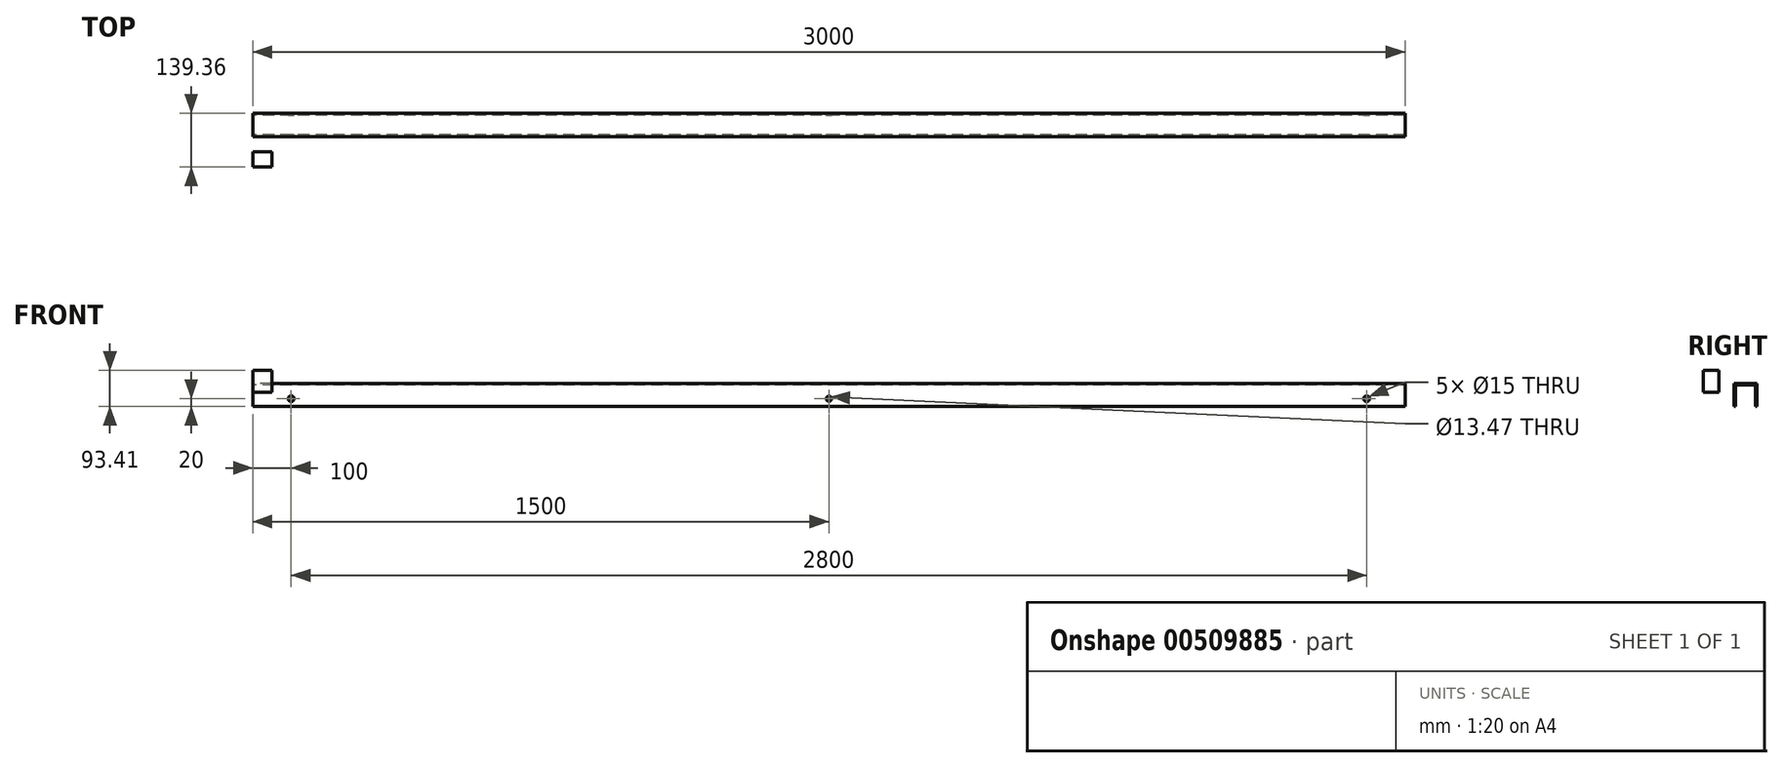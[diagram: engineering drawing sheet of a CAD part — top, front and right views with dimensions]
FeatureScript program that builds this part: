
annotation { "Feature Type Name" : "Feature", "Feature Type Description" : "" }
export const myFeature = defineFeature(function(context is Context, id is Id, definition is map)
    precondition{}
    {
        {
            var Q0;
            Q0=qCreatedBy(makeId("Right.planeOp"),FACE);
            var sketch = newSketch(context, id + "F0", { "sketchPlane" : qUnion([Q0])});
            skLineSegment(sketch, "E0", {"start": v(0, 0) * mm, "end": v(60, 0) * mm});
            skLineSegment(sketch, "E1", {"start": v(60, 0) * mm, "end": v(60, -60) * mm});
            skLineSegment(sketch, "E2", {"start": v(60, -60) * mm, "end": v(56, -60) * mm});
            skLineSegment(sketch, "E3", {"start": v(56, -60) * mm, "end": v(56, -4) * mm});
            skLineSegment(sketch, "E4", {"start": v(56, -4) * mm, "end": v(4, -4) * mm});
            skLineSegment(sketch, "E5", {"start": v(4, -4) * mm, "end": v(4, -60) * mm});
            skLineSegment(sketch, "E6", {"start": v(4, -60) * mm, "end": v(0, -60) * mm});
            skLineSegment(sketch, "E7", {"start": v(0, -60) * mm, "end": v(0, 0) * mm});
            skSolve(sketch);
        }
        {
            var Q0;
            Q0=makeQuery(id+"F0.imprint","IMPRINT",FACE,{"disambiguationData":[TD([[makeQuery(id+"F0.imprint","IMPRINT",EDGE,{"derivedFrom":sQuery(id+"F0.wireOp",EDGE,"E0")}),-1.0]])]});
            extrude(context, id + "F1", {"entities" : qUnion([Q0]), "depth" : 3000 * mm, "offsetDistance" : 25 * mm});
        }
        {
            var Q0;
            Q0=makeQuery(id+"F1.opExtrude","SWEPT_FACE",FACE,{"disambiguationData":[OSD([sQuery(id+"F0.wireOp",EDGE,"E1")])]});
            var sketch = newSketch(context, id + "F2", { "sketchPlane" : qUnion([Q0])});
            skCircle(sketch, "E8", {"center": v(-2900, -40) * mm, "radius": 7.5 * mm});
            skCircle(sketch, "E9", {"center": v(-1500, -40) * mm, "radius": 7.5 * mm});
            skCircle(sketch, "E10", {"center": v(-100, -40) * mm, "radius": 7.5 * mm});
            skSolve(sketch);
        }
        {
            var Q0;
            Q0=makeQuery(id+"F2.imprint","IMPRINT",FACE,{"disambiguationData":[TD([[makeQuery(id+"F2.imprint","IMPRINT",EDGE,{"derivedFrom":sQuery(id+"F2.wireOp",EDGE,"E10")}),1.0]])]});
            extrude(context, id + "F3", {"entities" : qUnion([Q0]), "operationType" : NewBodyOperationType.REMOVE, "oppositeDirection" : true, "depth" : 4 * mm, "offsetDistance" : 25 * mm});
        }
        {
            var Q0;
            Q0=makeQuery(id+"F1.opExtrude","SWEPT_FACE",FACE,{"disambiguationData":[OSD([sQuery(id+"F0.wireOp",EDGE,"E1")])]});
            var sketch = newSketch(context, id + "F4", { "sketchPlane" : qUnion([Q0])});
            skCircle(sketch, "E11", {"center": v(-2900, -40) * mm, "radius": 7.5 * mm});
            skSolve(sketch);
        }
        {
            var Q0;
            Q0=makeQuery(id+"F4.imprint","IMPRINT",FACE,{"disambiguationData":[TD([[makeQuery(id+"F4.imprint","IMPRINT",EDGE,{"derivedFrom":sQuery(id+"F4.wireOp",EDGE,"E11")}),1.0]])]});
            extrude(context, id + "F5", {"entities" : qUnion([Q0]), "operationType" : NewBodyOperationType.REMOVE, "oppositeDirection" : true, "depth" : 4 * mm, "offsetDistance" : 25 * mm});
        }
        {
            var Q0;
            Q0=makeQuery(id+"F1.opExtrude","SWEPT_FACE",FACE,{"disambiguationData":[OSD([sQuery(id+"F0.wireOp",EDGE,"E1")])]});
            var sketch = newSketch(context, id + "F6", { "sketchPlane" : qUnion([Q0])});
            skCircle(sketch, "E12", {"center": v(-1500, -40) * mm, "radius": 7.5 * mm});
            skSolve(sketch);
        }
        {
            var Q0;
            Q0=makeQuery(id+"F6.imprint","IMPRINT",FACE,{"disambiguationData":[TD([[makeQuery(id+"F6.imprint","IMPRINT",EDGE,{"derivedFrom":sQuery(id+"F6.wireOp",EDGE,"E12")}),1.0]])]});
            extrude(context, id + "F7", {"entities" : qUnion([Q0]), "operationType" : NewBodyOperationType.REMOVE, "oppositeDirection" : true, "depth" : 4 * mm, "offsetDistance" : 25 * mm});
        }
        {
            var Q0;
            Q0=makeQuery(id+"F1.opExtrude","SWEPT_FACE",FACE,{"disambiguationData":[OSD([sQuery(id+"F0.wireOp",EDGE,"E7")])]});
            var sketch = newSketch(context, id + "F8", { "sketchPlane" : qUnion([Q0])});
            skCircle(sketch, "E13", {"center": v(100, -40) * mm, "radius": 7.5 * mm});
            skSolve(sketch);
        }
        {
            var Q0;
            Q0=makeQuery(id+"F8.imprint","IMPRINT",FACE,{"disambiguationData":[TD([[makeQuery(id+"F8.imprint","IMPRINT",EDGE,{"derivedFrom":sQuery(id+"F8.wireOp",EDGE,"E13")}),1.0]])]});
            extrude(context, id + "F9", {"entities" : qUnion([Q0]), "operationType" : NewBodyOperationType.REMOVE, "oppositeDirection" : true, "depth" : 4 * mm, "offsetDistance" : 25 * mm});
        }
        {
            var Q0;
            Q0=makeQuery(id+"F1.opExtrude","SWEPT_FACE",FACE,{"disambiguationData":[OSD([sQuery(id+"F0.wireOp",EDGE,"E7")])]});
            var sketch = newSketch(context, id + "F10", { "sketchPlane" : qUnion([Q0])});
            skCircle(sketch, "E14", {"center": v(1500, -40) * mm, "radius": 6.74 * mm});
            skSolve(sketch);
        }
        {
            var Q0;
            Q0=makeQuery(id+"F10.imprint","IMPRINT",FACE,{"disambiguationData":[TD([[makeQuery(id+"F10.imprint","IMPRINT",EDGE,{"derivedFrom":sQuery(id+"F10.wireOp",EDGE,"E14")}),1.0]])]});
            extrude(context, id + "F11", {"entities" : qUnion([Q0]), "operationType" : NewBodyOperationType.REMOVE, "oppositeDirection" : true, "depth" : 4 * mm, "offsetDistance" : 25 * mm});
        }
        {
            var Q0;
            Q0=makeQuery(id+"F1.opExtrude","SWEPT_FACE",FACE,{"disambiguationData":[OSD([sQuery(id+"F0.wireOp",EDGE,"E7")])]});
            var sketch = newSketch(context, id + "F12", { "sketchPlane" : qUnion([Q0])});
            skCircle(sketch, "E15", {"center": v(2900, -40) * mm, "radius": 7.5 * mm});
            skSolve(sketch);
        }
        {
            var Q0;
            Q0=makeQuery(id+"F12.imprint","IMPRINT",FACE,{"disambiguationData":[TD([[makeQuery(id+"F12.imprint","IMPRINT",EDGE,{"derivedFrom":sQuery(id+"F12.wireOp",EDGE,"E15")}),1.0]])]});
            extrude(context, id + "F13", {"entities" : qUnion([Q0]), "operationType" : NewBodyOperationType.REMOVE, "oppositeDirection" : true, "depth" : 4 * mm, "offsetDistance" : 25 * mm});
        }
        {
            var Q0;
            Q0=qCreatedBy(makeId("Right.planeOp"),FACE);
            var sketch = newSketch(context, id + "F14", { "sketchPlane" : qUnion([Q0])});
            skLineSegment(sketch, "E16.bottom", {"start": v(-39.36, -22.6) * mm, "end": v(-79.36, -22.6) * mm});
            skLineSegment(sketch, "E16.top", {"start": v(-39.36, 33.4) * mm, "end": v(-79.36, 33.4) * mm});
            skLineSegment(sketch, "E16.left", {"start": v(-39.36, -22.6) * mm, "end": v(-39.36, 33.4) * mm});
            skLineSegment(sketch, "E16.right", {"start": v(-79.36, -22.6) * mm, "end": v(-79.36, 33.4) * mm});
            skPoint(sketch, "E16.middle", {"position": v(-59.36, 5.4) * mm});
            skSolve(sketch);
        }
        {
            var Q0;
            Q0=makeQuery(id+"F14.imprint","IMPRINT",FACE,{"disambiguationData":[TD([[makeQuery(id+"F14.imprint","IMPRINT",EDGE,{"derivedFrom":sQuery(id+"F14.wireOp",EDGE,"E16.bottom")}),-1.0]])]});
            extrude(context, id + "F15", {"entities" : qUnion([Q0]), "depth" : 50 * mm, "offsetDistance" : 25 * mm});
        }
    });
